FCSTD DOCUMENT  (FreeCAD 0.20R29603 (Git))
Label: airfoil_import
License: All rights reserved
LicenseURL: http://en.wikipedia.org/wiki/All_rights_reserved
objects: Sketcher::SketchObject×1
note: 1 computed .brp shape members not serialized (recipe doc carries the construction recipe); baked Part::Feature solids carry a one-line shape summary decoded from their .brp

FEATURE [Sketcher::SketchObject] Sketch
  FullyConstrained = true
  sketch-geometry (5):
    g0: LineSegment StartX=0 StartY=0 StartZ=0 EndX=15 EndY=0 EndZ=0
    g1: LineSegment StartX=0 StartY=-16 StartZ=0 EndX=15 EndY=-16 EndZ=0
    g2: LineSegment StartX=0 StartY=0 StartZ=0 EndX=0 EndY=-16 EndZ=0
    g3: LineSegment StartX=15 StartY=0 StartZ=0 EndX=15 EndY=-16 EndZ=0
    g4: LineSegment StartX=7.5 StartY=2 StartZ=0 EndX=7.5 EndY=-18 EndZ=0
  constraints (15):
    c: Horizontal(g0)
    c: Horizontal(g1)
    c: Coincident(g2,g0)
    c: Coincident(g2,g1)
    c: Vertical(g2)
    c: Coincident(g3,g0)
    c: Coincident(g3,g1)
    c: Vertical(g3)
    c: DistanceY(g3,g3) = 16
    c: DistanceX(g0,g0) = 15
    c: Coincident(g0,g-1)
    c: Vertical(g4)
    c: DistanceY(g4,g4) = 20
    c: DistanceY(g0,g4) = 2
    c: DistanceX(g0,g4) = 7.5
